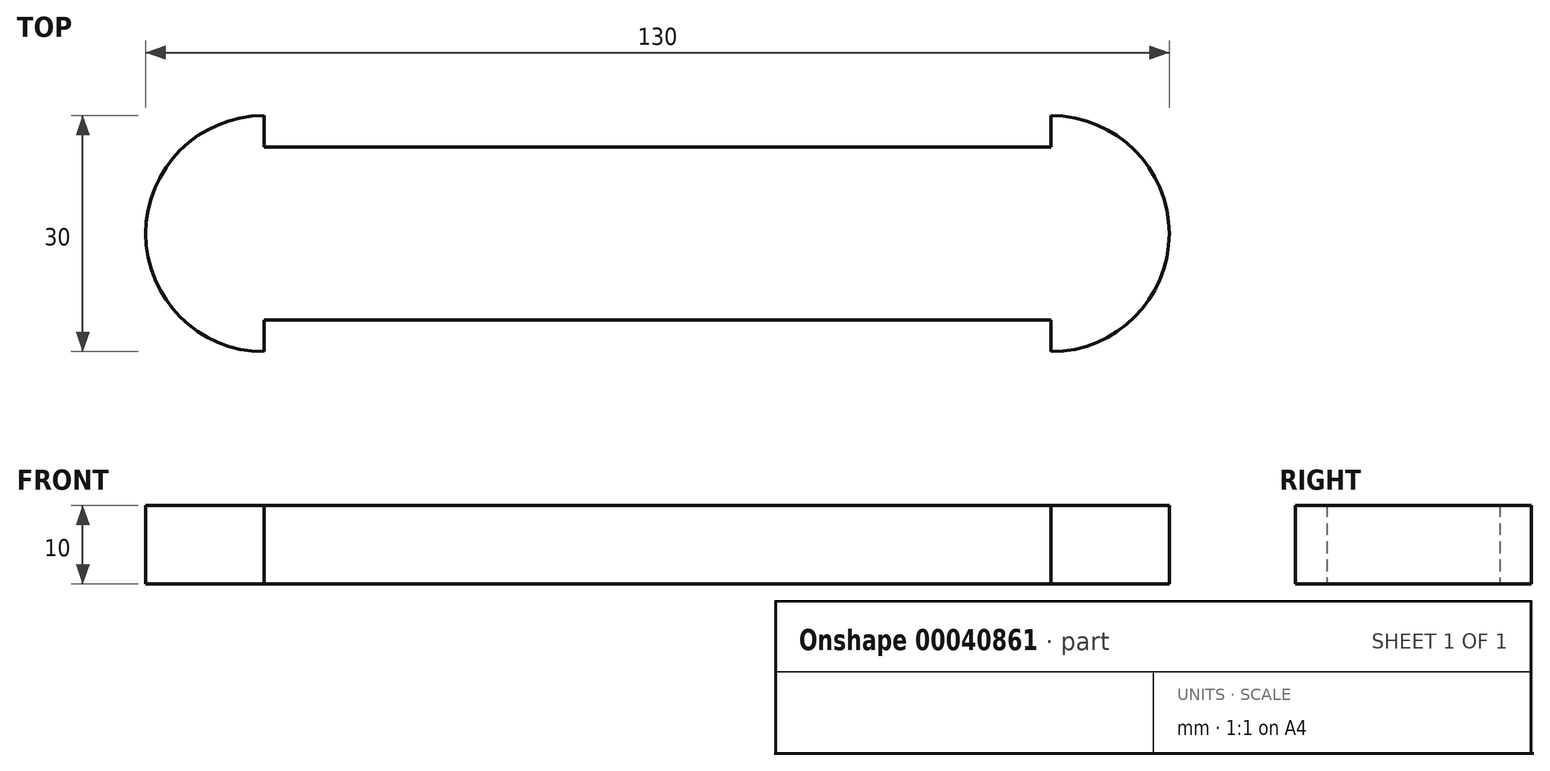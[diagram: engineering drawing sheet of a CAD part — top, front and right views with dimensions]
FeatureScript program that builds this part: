
annotation { "Feature Type Name" : "Feature", "Feature Type Description" : "" }
export const myFeature = defineFeature(function(context is Context, id is Id, definition is map)
    precondition{}
    {
        {
            var Q0;
            Q0=qCreatedBy(makeId("Top.planeOp"),FACE);
            var sketch = newSketch(context, id + "F0", { "sketchPlane" : qUnion([Q0])});
            skLineSegment(sketch, "E0.bottom", {"start": v(-38.18, 12.5) * mm, "end": v(61.82, 12.5) * mm});
            skLineSegment(sketch, "E0.top", {"start": v(-38.18, -9.5) * mm, "end": v(61.82, -9.5) * mm});
            skLineSegment(sketch, "E0.left", {"start": v(-38.18, 12.5) * mm, "end": v(-38.18, -9.5) * mm});
            skLineSegment(sketch, "E0.right", {"start": v(61.82, 12.5) * mm, "end": v(61.82, -9.5) * mm});
            skArc(sketch, "E1", {"start": v(61.82, -13.5) * mm, "mid": v(76.82, 1.5) * mm, "end": v(61.82, 16.5) * mm});
            skArc(sketch, "E2", {"start": v(-38.18, 16.5) * mm, "mid": v(-53.18, 1.5) * mm, "end": v(-38.18, -13.5) * mm});
            skLineSegment(sketch, "E3", {"start": v(-38.18, 16.5) * mm, "end": v(-38.18, -13.5) * mm});
            skLineSegment(sketch, "E4", {"start": v(61.82, 16.5) * mm, "end": v(61.82, -13.5) * mm});
            skSolve(sketch);
        }
        {
            var Q0;
            Q0 = qSketchRegion(id + "F0", true);
            extrude(context, id + "F1", {"entities" : qUnion([Q0]), "depth" : 10 * mm});
        }
    });
